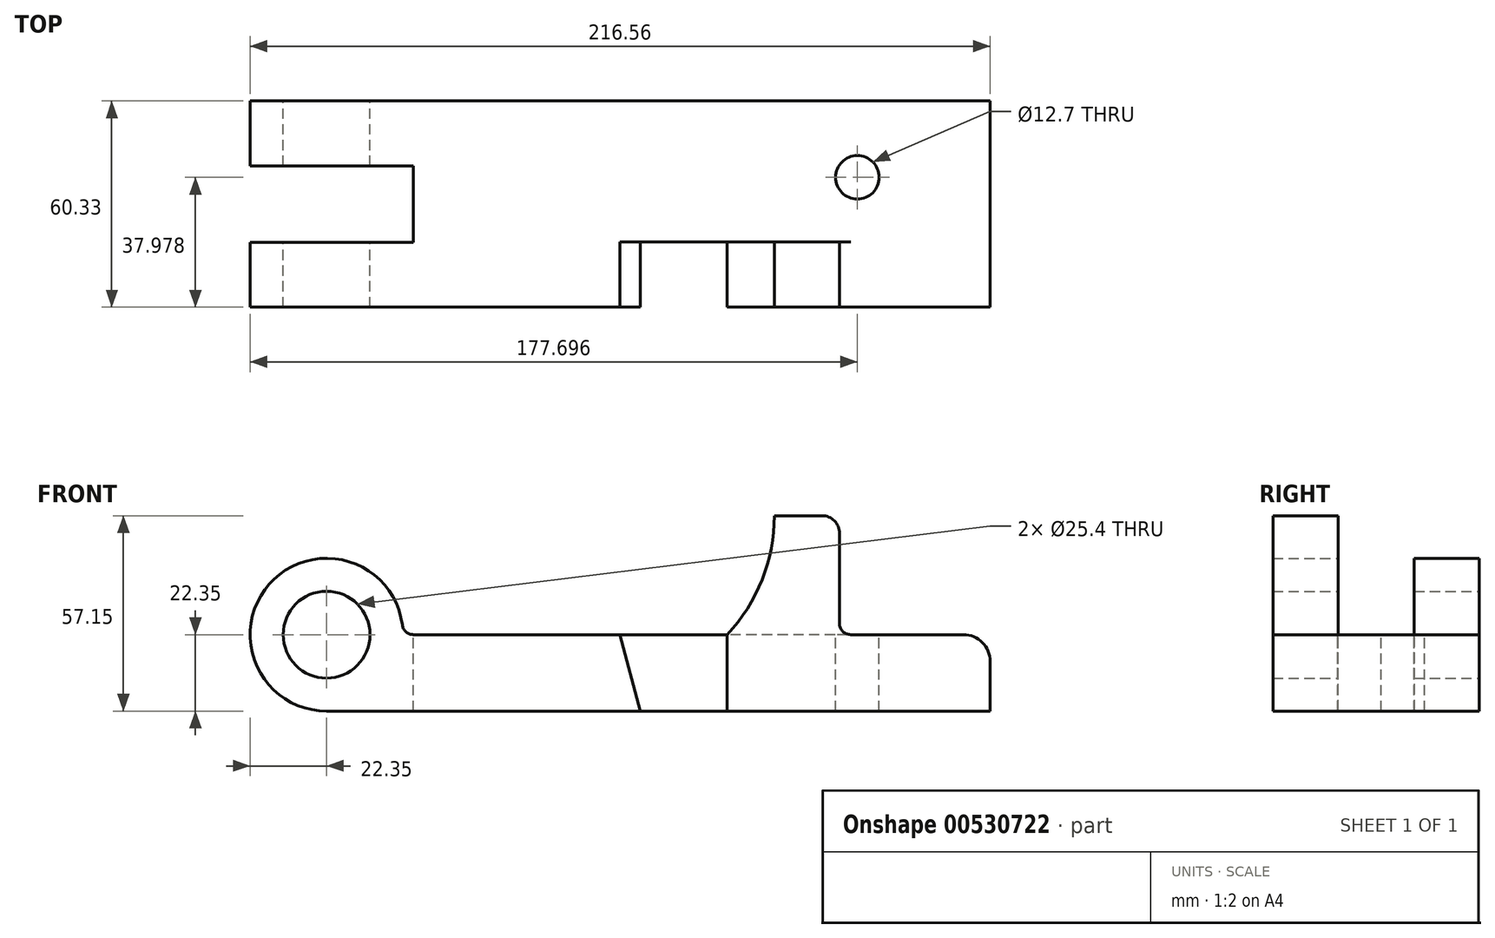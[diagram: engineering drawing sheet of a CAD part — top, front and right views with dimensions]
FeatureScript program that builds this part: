
annotation { "Feature Type Name" : "Feature", "Feature Type Description" : "" }
export const myFeature = defineFeature(function(context is Context, id is Id, definition is map)
    precondition{}
    {
        {
            var Q0;
            Q0=qCreatedBy(makeId("Front.planeOp"),FACE);
            var sketch = newSketch(context, id + "F0", { "sketchPlane" : qUnion([Q0])});
            skCircle(sketch, "E0", {"center": v(0, 0) * mm, "radius": 12.7 * mm});
            skArc(sketch, "E1", {"start": v(22.17, 2.88) * mm, "mid": v(-16.8, 14.75) * mm, "end": v(0, -22.35) * mm});
            skLineSegment(sketch, "E2", {"start": v(0, -22.35) * mm, "end": v(194.2, -22.35) * mm});
            skLineSegment(sketch, "E3", {"start": v(25.44, 0) * mm, "end": v(117.25, 0) * mm});
            skLineSegment(sketch, "E4", {"start": v(91.85, -22.35) * mm, "end": v(85.85, 0) * mm});
            skLineSegment(sketch, "E5", {"start": v(194.2, -22.35) * mm, "end": v(194.2, -7.87) * mm});
            skLineSegment(sketch, "E6", {"start": v(0, 34.8) * mm, "end": v(145, 34.8) * mm});
            skLineSegment(sketch, "E7", {"start": v(0, 34.8) * mm, "end": v(131.04, 34.8) * mm});
            skArc(sketch, "E8", {"start": v(117.25, 0) * mm, "mid": v(127.46, 16.08) * mm, "end": v(131.04, 34.8) * mm});
            skLineSegment(sketch, "E9", {"start": v(153.4, 0) * mm, "end": v(186.33, 0) * mm});
            skLineSegment(sketch, "E10", {"start": v(150.09, 29.72) * mm, "end": v(150.09, 3.3) * mm});
            skLineSegment(sketch, "E11", {"start": v(117.25, 0) * mm, "end": v(117.25, -22.35) * mm});
            skPoint(sketch, "E12.visualSharp", {"position": v(150.09, 0) * mm});
            skArc(sketch, "E12.filletArc", {"start": v(150.09, 3.3) * mm, "mid": v(151.06, 0.97) * mm, "end": v(153.4, 0) * mm});
            skPoint(sketch, "E13.visualSharp", {"position": v(150.09, 34.8) * mm});
            skArc(sketch, "E13.filletArc", {"start": v(150.09, 29.72) * mm, "mid": v(148.6, 33.31) * mm, "end": v(145, 34.8) * mm});
            skPoint(sketch, "E14.visualSharp", {"position": v(194.2, 0) * mm});
            skArc(sketch, "E14.filletArc", {"start": v(194.2, -7.87) * mm, "mid": v(191.9, -2.3) * mm, "end": v(186.33, 0) * mm});
            skPoint(sketch, "E15.visualSharp", {"position": v(22.35, 0) * mm});
            skArc(sketch, "E15.filletArc", {"start": v(22.17, 2.88) * mm, "mid": v(23.26, 0.82) * mm, "end": v(25.44, 0) * mm});
            skLineSegment(sketch, "E16", {"start": v(0, 0) * mm, "end": v(-22.35, 0) * mm});
            skSolve(sketch);
        }
        {
            var Q0;
            {var subQ0=sQuery(id+"F0.wireOp",EDGE,"E5");Q0=makeQuery(id+"F0.imprint","IMPRINT",FACE,{"disambiguationData":[TD([[makeQuery(id+"F0.imprint","IMPRINT",EDGE,{"derivedFrom":subQ0}),1.0]])]});}
            var Q1;
            {var subQ0=sQuery(id+"F0.wireOp",EDGE,"E4");Q1=makeQuery(id+"F0.imprint","IMPRINT",FACE,{"disambiguationData":[TD([[makeQuery(id+"F0.imprint","IMPRINT",EDGE,{"derivedFrom":subQ0}),-1.0]])]});}
            var Q2;
            Q2=makeQuery(id+"F0.imprint","IMPRINT",FACE,{"disambiguationData":[TD([[makeQuery(id+"F0.imprint","IMPRINT",EDGE,{"derivedFrom":sQuery(id+"F0.wireOp",EDGE,"E0")}),-1.0]])]});
            extrude(context, id + "F1", {"entities" : qUnion([Q0, Q1, Q2]), "depth" : 60.32 * mm});
        }
        {
            var Q0;
            Q0=makeQuery(id+"F1.opExtrude","SWEPT_FACE",FACE,{"disambiguationData":[OSD([sQuery(id+"F0.wireOp",EDGE,"E3")])]});
            var sketch = newSketch(context, id + "F2", { "sketchPlane" : qUnion([Q0])});
            skLineSegment(sketch, "E17.0", {"start": v(22.35, -60.33) * mm, "end": v(117.25, -60.33) * mm});
            skLineSegment(sketch, "E18", {"start": v(-23.99, -19) * mm, "end": v(25.44, -19) * mm});
            skLineSegment(sketch, "E19", {"start": v(-23.27, -41.33) * mm, "end": v(25.44, -41.33) * mm});
            skLineSegment(sketch, "E20", {"start": v(25.44, -19) * mm, "end": v(25.44, -41.33) * mm});
            skLineSegment(sketch, "E21", {"start": v(-23.99, -19) * mm, "end": v(-23.99, -41.33) * mm});
            skLineSegment(sketch, "E22", {"start": v(-23.99, -41.33) * mm, "end": v(-23.27, -41.33) * mm});
            skSolve(sketch);
        }
        {
            var Q0;
            Q0=qSketchRegion(id+"F2",true);
            extrude(context, id + "F3", {"entities" : qUnion([Q0]), "operationType" : NewBodyOperationType.REMOVE, "endBound" : BoundingType.SYMMETRIC, "oppositeDirection" : true, "depth" : 127.5 * mm});
        }
        {
            var Q0;
            Q0=makeQuery(id+"F1.opExtrude","SWEPT_FACE",FACE,{"disambiguationData":[OSD([sQuery(id+"F0.wireOp",EDGE,"E6")])]});
            var sketch = newSketch(context, id + "F4", { "sketchPlane" : qUnion([Q0])});
            skLineSegment(sketch, "E23", {"start": v(91.7, -60.33) * mm, "end": v(153.4, -60.33) * mm});
            skLineSegment(sketch, "E24", {"start": v(153.4, -60.33) * mm, "end": v(153.4, -41.28) * mm});
            skLineSegment(sketch, "E25", {"start": v(153.4, -41.27) * mm, "end": v(91.7, -41.27) * mm});
            skLineSegment(sketch, "E26", {"start": v(91.7, -41.28) * mm, "end": v(91.7, -60.33) * mm});
            skLineSegment(sketch, "E27.0", {"start": v(153.4, -60.33) * mm, "end": v(153.4, 0) * mm});
            skLineSegment(sketch, "E28", {"start": v(91.7, -41.27) * mm, "end": v(91.7, 0) * mm});
            skLineSegment(sketch, "E29", {"start": v(91.7, 0) * mm, "end": v(153.4, 0) * mm});
            skSolve(sketch);
        }
        {
            var Q0;
            {var subQ0=sQuery(id+"F4.wireOp",EDGE,"E28");Q0=makeQuery(id+"F4.imprint","IMPRINT",FACE,{"disambiguationData":[TD([[makeQuery(id+"F4.imprint","IMPRINT",EDGE,{"derivedFrom":subQ0}),-1.0]])]});}
            var Q1;
            {var subQ0=sQuery(id+"F4.wireOp",EDGE,"E25");var subQ1=sQuery(id+"F0.wireOp",EDGE,"E6");var subQ2=makeQuery(id+"F1.opExtrude","SWEPT_EDGE",EDGE,{"disambiguationData":[OSD([subQ1,sQuery(id+"F0.wireOp",EDGE,"E13.filletArc")])]});var subQ3=makeQuery(id+"F4.imprint","INTERSECT",VERTEX,{"derivedFrom":[subQ2,subQ0]});Q1=makeQuery(id+"F4.imprint","IMPRINT",FACE,{"disambiguationData":[TD([[makeQuery(id+"F4.imprint","IMPRINT",EDGE,{"disambiguationData":[TD([[subQ3,-1.0]])],"derivedFrom":subQ0}),-1.0]])]});}
            var Q2;
            {var subQ0=sQuery(id+"F4.wireOp",EDGE,"E27.0");var subQ1=sQuery(id+"F4.wireOp",EDGE,"E25");var subQ2=makeQuery(id+"F4.imprint","INTERSECT",VERTEX,{"derivedFrom":[subQ1,subQ0]});Q2=makeQuery(id+"F4.imprint","IMPRINT",FACE,{"disambiguationData":[TD([[makeQuery(id+"F4.imprint","IMPRINT",EDGE,{"disambiguationData":[TD([[subQ2,-1.0]])],"derivedFrom":subQ0}),1.0]])]});}
            extrude(context, id + "F5", {"entities" : qUnion([Q0, Q1, Q2]), "operationType" : NewBodyOperationType.REMOVE, "oppositeDirection" : true, "depth" : 34.8 * mm});
        }
        {
            var Q0;
            Q0=makeQuery(id+"F5.boolean.opBoolean","MERGE",FACE,{"derivedFrom":[makeQuery(id+"F1.opExtrude","SWEPT_FACE",FACE,{"disambiguationData":[OSD([sQuery(id+"F0.wireOp",EDGE,"E3")])]}),makeQuery(id+"F1.opExtrude","SWEPT_FACE",FACE,{"disambiguationData":[OSD([sQuery(id+"F0.wireOp",EDGE,"E9")])]}),makeQuery(id+"F5.opExtrude","CAP_FACE",FACE,{"disambiguationData":[OSD([sQuery(id+"F4.wireOp",EDGE,"E25"),sQuery(id+"F4.wireOp",EDGE,"E27.0"),sQuery(id+"F4.wireOp",EDGE,"E28"),sQuery(id+"F4.wireOp",EDGE,"E29")])],"isStart":false})]});
            var sketch = newSketch(context, id + "F6", { "sketchPlane" : qUnion([Q0])});
            skLineSegment(sketch, "E30.0", {"start": v(25.44, 0) * mm, "end": v(186.33, 0) * mm});
            skPoint(sketch, "E31.0", {"position": v(191.9, 0) * mm});
            skLineSegment(sketch, "E32.0", {"start": v(194.2, 0) * mm, "end": v(186.33, 0) * mm});
            skLineSegment(sketch, "E33", {"start": v(194.2, 0) * mm, "end": v(155.35, 0) * mm});
            skLineSegment(sketch, "E34", {"start": v(194.2, 0) * mm, "end": v(194.2, -22.35) * mm});
            skLineSegment(sketch, "E35", {"start": v(155.35, 0) * mm, "end": v(155.35, -22.35) * mm});
            skCircle(sketch, "E36", {"center": v(155.35, -22.35) * mm, "radius": 6.35 * mm});
            skSolve(sketch);
        }
        {
            var Q0;
            Q0=qSketchRegion(id+"F6",true);
            extrude(context, id + "F7", {"entities" : qUnion([Q0]), "operationType" : NewBodyOperationType.REMOVE, "endBound" : BoundingType.THROUGH_ALL, "oppositeDirection" : true, "depth" : 25.4 * mm});
        }
        {
            var Q0;
            Q0=makeQuery(id+"F1.opExtrude","CAP_FACE",FACE,{"disambiguationData":[OSD([sQuery(id+"F0.wireOp",EDGE,"E0"),sQuery(id+"F0.wireOp",EDGE,"E1"),sQuery(id+"F0.wireOp",EDGE,"E2"),sQuery(id+"F0.wireOp",EDGE,"E3"),sQuery(id+"F0.wireOp",EDGE,"E5"),sQuery(id+"F0.wireOp",EDGE,"E6"),sQuery(id+"F0.wireOp",EDGE,"E8"),sQuery(id+"F0.wireOp",EDGE,"E9"),sQuery(id+"F0.wireOp",EDGE,"E10"),sQuery(id+"F0.wireOp",EDGE,"E12.filletArc"),sQuery(id+"F0.wireOp",EDGE,"E13.filletArc"),sQuery(id+"F0.wireOp",EDGE,"E14.filletArc")])],"isStart":false});
            var sketch = newSketch(context, id + "F8", { "sketchPlane" : qUnion([Q0])});
            skLineSegment(sketch, "E37.0.0", {"start": v(117.25, -22.35) * mm, "end": v(117.25, 0) * mm});
            skLineSegment(sketch, "E37.0.1", {"start": v(117.25, 0) * mm, "end": v(85.85, 0) * mm});
            skLineSegment(sketch, "E37.0.2", {"start": v(85.85, 0) * mm, "end": v(91.85, -22.35) * mm});
            skLineSegment(sketch, "E37.0.3", {"start": v(91.85, -22.35) * mm, "end": v(117.25, -22.35) * mm});
            skSolve(sketch);
        }
        {
            var Q0;
            Q0=qSketchRegion(id+"F8",true);
            extrude(context, id + "F9", {"entities" : qUnion([Q0]), "operationType" : NewBodyOperationType.REMOVE, "oppositeDirection" : true, "depth" : 19.05 * mm});
        }
    });
